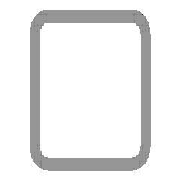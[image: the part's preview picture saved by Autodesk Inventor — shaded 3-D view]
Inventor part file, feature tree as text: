
AUTODESK INVENTOR PART (.ipt)
format: ipt  version: 2025 (Build 290162010, 162A)  size: 133,120 bytes
history: native  units: mm (DEFAULTED — no unit token found)
features: other x4, sketch x1, plane x1
ambient origin geometry x8: Origin, YZ Plane, XZ Plane, XY Plane, X Axis, Y Axis, Z Axis, Center Point
bodies: Solid1 (feature_tree), Body (feature_tree)
feature tree (6):
  parser-record x1  (decoder bookkeeping rows leaked as tree rows — omitted from the tree; the rows remain in map.json)
  other  "Driven Length"
  other  "Start Plane"
  other  "End Plane"
  sketch  "Sketch3"  dims[d3=1170.0mm d4=0.0mm d7=6.0mm d9=80.0mm d11=80.0mm d12=3.0mm d13=40.0mm d14=1210.0mm d15=40.0mm d16=40.0mm d17=90.0deg d18=1170.0mm]
  plane  "Work Plane3"
